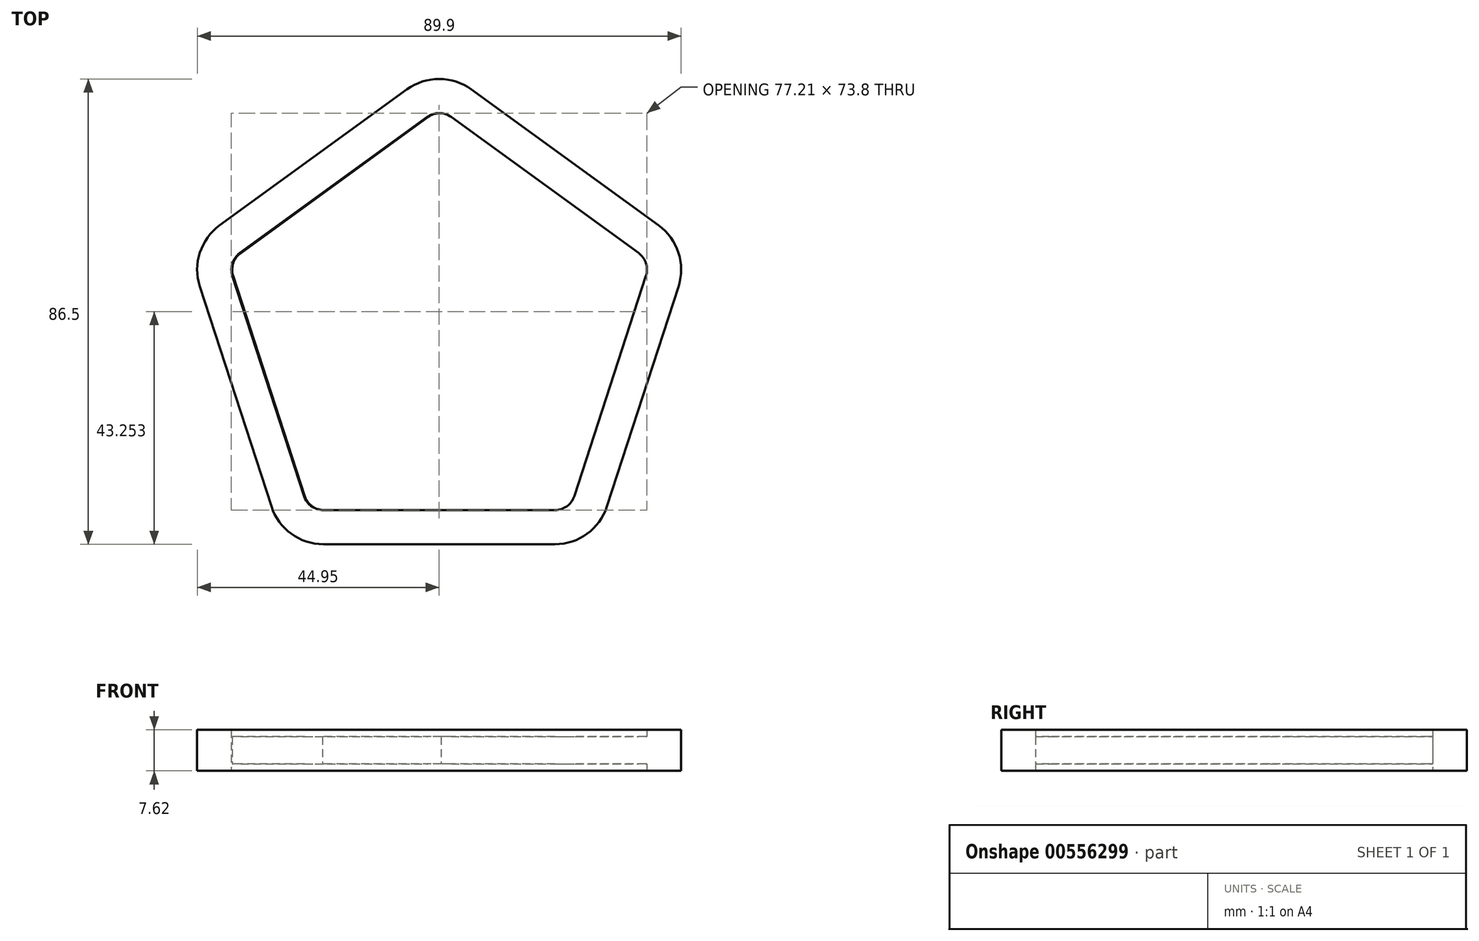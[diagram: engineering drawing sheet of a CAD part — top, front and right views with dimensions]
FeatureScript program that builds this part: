
annotation { "Feature Type Name" : "Feature", "Feature Type Description" : "" }
export const myFeature = defineFeature(function(context is Context, id is Id, definition is map)
    precondition{}
    {
        {
            var Q0;
            Q0=qCreatedBy(makeId("Top.planeOp"),FACE);
            var sketch = newSketch(context, id + "F0", { "sketchPlane" : qUnion([Q0])});
            skCircle(sketch, "E0.cCircle", {"center": v(0, 0) * mm, "radius": 39.76 * mm, "construction": true});
            skLineSegment(sketch, "E0.0", {"start": v(5.97, 44.8) * mm, "end": v(40.77, 19.52) * mm});
            skLineSegment(sketch, "E0.1", {"start": v(44.46, 8.17) * mm, "end": v(31.17, -32.74) * mm});
            skLineSegment(sketch, "E0.2", {"start": v(21.5, -39.76) * mm, "end": v(-21.5, -39.76) * mm});
            skLineSegment(sketch, "E0.3", {"start": v(-31.17, -32.74) * mm, "end": v(-44.46, 8.17) * mm});
            skLineSegment(sketch, "E0.4", {"start": v(-40.77, 19.52) * mm, "end": v(-5.97, 44.8) * mm});
            skPoint(sketch, "E0.0.midPoint", {"position": v(23.37, 32.16) * mm});
            skPoint(sketch, "E1.visualSharp", {"position": v(-46.74, 15.19) * mm});
            skArc(sketch, "E1.filletArc", {"start": v(-40.77, 19.52) * mm, "mid": v(-44.46, 14.44) * mm, "end": v(-44.46, 8.17) * mm});
            skPoint(sketch, "E2.visualSharp", {"position": v(0, 49.14) * mm});
            skArc(sketch, "E2.filletArc", {"start": v(5.97, 44.8) * mm, "mid": v(0, 46.74) * mm, "end": v(-5.97, 44.8) * mm});
            skPoint(sketch, "E3.visualSharp", {"position": v(46.74, 15.19) * mm});
            skArc(sketch, "E3.filletArc", {"start": v(44.46, 8.17) * mm, "mid": v(44.46, 14.44) * mm, "end": v(40.77, 19.52) * mm});
            skPoint(sketch, "E4.visualSharp", {"position": v(28.89, -39.76) * mm});
            skArc(sketch, "E4.filletArc", {"start": v(21.5, -39.76) * mm, "mid": v(27.48, -37.82) * mm, "end": v(31.17, -32.74) * mm});
            skPoint(sketch, "E5.visualSharp", {"position": v(-28.89, -39.76) * mm});
            skArc(sketch, "E5.filletArc", {"start": v(-31.17, -32.74) * mm, "mid": v(-27.48, -37.82) * mm, "end": v(-21.5, -39.76) * mm});
            skLineSegment(sketch, "E6.0", {"start": v(-25.13, -30.77) * mm, "end": v(-38.42, 10.13) * mm});
            skArc(sketch, "E6.1", {"start": v(-25.13, -30.77) * mm, "mid": v(-23.74, -32.68) * mm, "end": v(-21.5, -33.4) * mm});
            skLineSegment(sketch, "E6.2", {"start": v(21.5, -33.4) * mm, "end": v(-21.5, -33.4) * mm});
            skArc(sketch, "E6.3", {"start": v(21.5, -33.4) * mm, "mid": v(23.74, -32.68) * mm, "end": v(25.13, -30.77) * mm});
            skLineSegment(sketch, "E6.4", {"start": v(38.42, 10.13) * mm, "end": v(25.13, -30.77) * mm});
            skLineSegment(sketch, "E6.5", {"start": v(-37.03, 14.39) * mm, "end": v(-2.24, 39.67) * mm});
            skArc(sketch, "E6.6", {"start": v(2.24, 39.67) * mm, "mid": v(0, 40.4) * mm, "end": v(-2.24, 39.67) * mm});
            skLineSegment(sketch, "E6.7", {"start": v(2.24, 39.67) * mm, "end": v(37.03, 14.39) * mm});
            skArc(sketch, "E6.8", {"start": v(38.42, 10.13) * mm, "mid": v(38.42, 12.48) * mm, "end": v(37.03, 14.39) * mm});
            skArc(sketch, "E7.3", {"start": v(-37.03, 14.39) * mm, "mid": v(-38.42, 12.48) * mm, "end": v(-38.42, 10.13) * mm});
            skSolve(sketch);
        }
        {
            var Q0;
            Q0 = qSketchRegion(id + "F0", true);
            extrude(context, id + "F1", {"entities" : qUnion([Q0]), "depth" : 7.62 * mm, "offsetDistance" : 25.4 * mm});
        }
        {
            var Q0;
            Q0=qCreatedBy(makeId("Top.planeOp"),FACE);
            cPlane(context, id + "F2", {"entities" : qUnion([Q0]), "cplaneType" : CPlaneType.OFFSET, "offset" : 1.27 * mm, "width" : 152.4 * mm, "height" : 152.4 * mm});
        }
        {
            var Q0;
            Q0=qCreatedBy(id+"F2.planeOp",FACE);
            var sketch = newSketch(context, id + "F3", { "sketchPlane" : qUnion([Q0])});
            skLineSegment(sketch, "E8.0", {"start": v(-24.98, -30.79) * mm, "end": v(-38.27, 10.12) * mm});
            skArc(sketch, "E8.1", {"start": v(-24.98, -30.79) * mm, "mid": v(-23.6, -32.7) * mm, "end": v(-21.35, -33.42) * mm});
            skLineSegment(sketch, "E8.2", {"start": v(21.65, -33.42) * mm, "end": v(-21.35, -33.42) * mm});
            skArc(sketch, "E8.3", {"start": v(21.65, -33.42) * mm, "mid": v(23.9, -32.7) * mm, "end": v(25.28, -30.79) * mm});
            skLineSegment(sketch, "E8.4", {"start": v(38.57, 10.12) * mm, "end": v(25.28, -30.79) * mm});
            skLineSegment(sketch, "E8.5", {"start": v(-36.88, 14.38) * mm, "end": v(-2.09, 39.66) * mm});
            skArc(sketch, "E8.6", {"start": v(2.39, 39.66) * mm, "mid": v(0.15, 40.38) * mm, "end": v(-2.09, 39.66) * mm});
            skLineSegment(sketch, "E8.7", {"start": v(2.39, 39.66) * mm, "end": v(37.18, 14.38) * mm});
            skArc(sketch, "E8.8", {"start": v(38.57, 10.12) * mm, "mid": v(38.57, 12.47) * mm, "end": v(37.18, 14.38) * mm});
            skArc(sketch, "E9.3", {"start": v(-36.88, 14.38) * mm, "mid": v(-38.27, 12.47) * mm, "end": v(-38.27, 10.12) * mm});
            skSolve(sketch);
        }
        {
            var Q0;
            Q0 = qSketchRegion(id + "F3", true);
            extrude(context, id + "F4", {"entities" : qUnion([Q0]), "operationType" : NewBodyOperationType.ADD, "depth" : 5.08 * mm, "offsetDistance" : 25.4 * mm});
        }
    });
